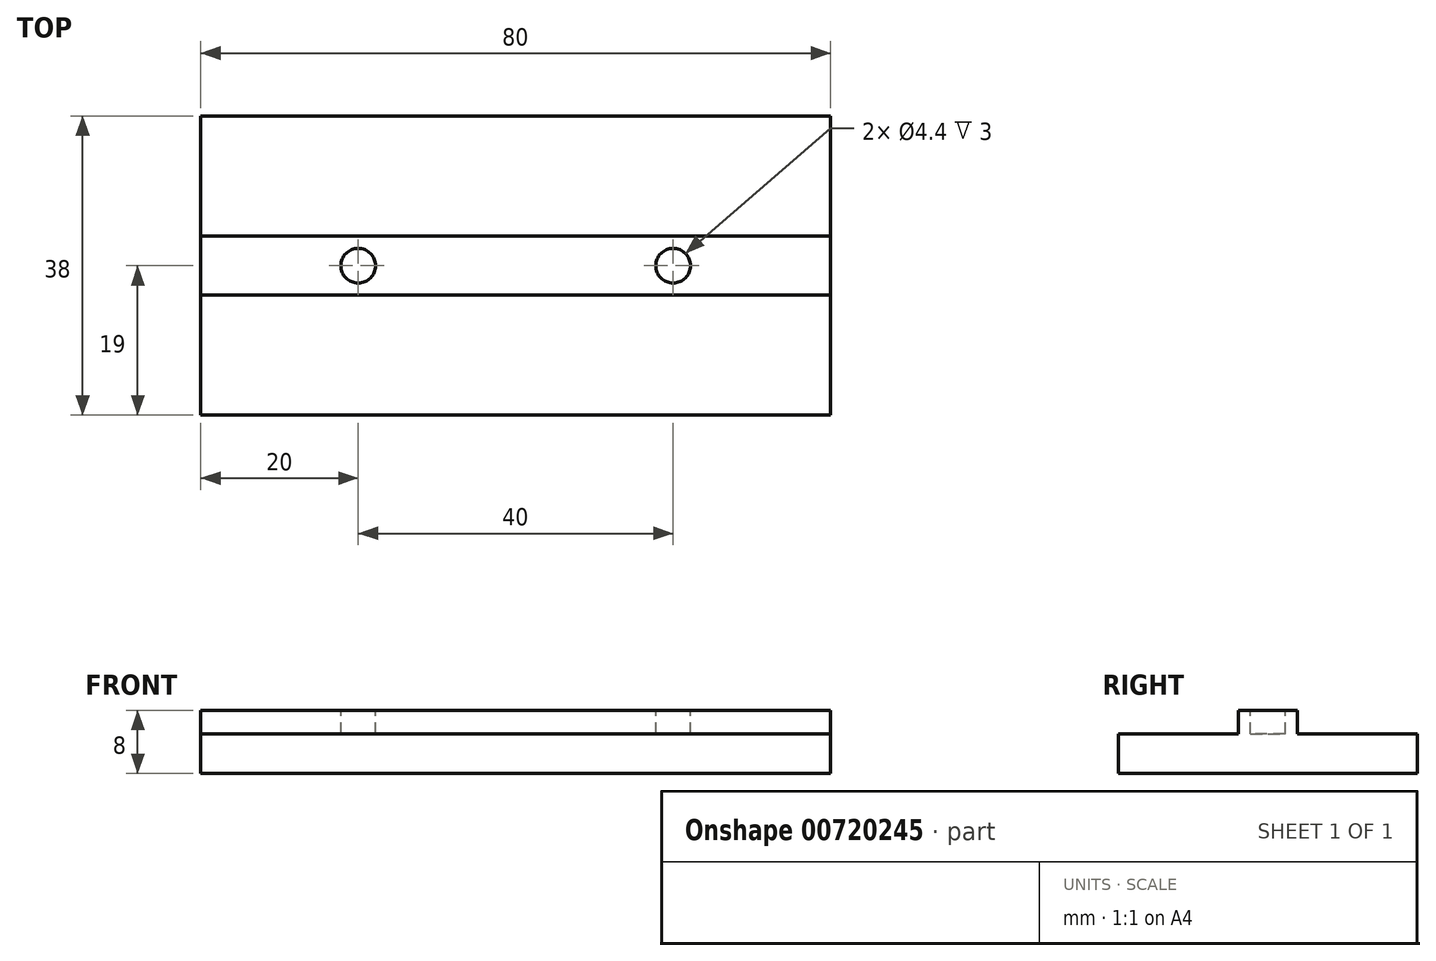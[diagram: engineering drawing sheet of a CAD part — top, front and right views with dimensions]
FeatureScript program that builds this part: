
annotation { "Feature Type Name" : "Feature", "Feature Type Description" : "" }
export const myFeature = defineFeature(function(context is Context, id is Id, definition is map)
    precondition{}
    {
        {
            var Q0;
            Q0=qCreatedBy(makeId("Top.planeOp"),FACE);
            var sketch = newSketch(context, id + "F0", { "sketchPlane" : qUnion([Q0])});
            skLineSegment(sketch, "E0.bottom", {"start": v(40, 19) * mm, "end": v(-40, 19) * mm});
            skLineSegment(sketch, "E0.top", {"start": v(40, -19) * mm, "end": v(-40, -19) * mm});
            skLineSegment(sketch, "E0.left", {"start": v(40, 19) * mm, "end": v(40, -19) * mm});
            skLineSegment(sketch, "E0.right", {"start": v(-40, 19) * mm, "end": v(-40, -19) * mm});
            skPoint(sketch, "E0.middle", {"position": v(0, 0) * mm});
            skLineSegment(sketch, "E1.bottom", {"start": v(40, 3.75) * mm, "end": v(-40, 3.75) * mm});
            skLineSegment(sketch, "E1.top", {"start": v(40, -3.75) * mm, "end": v(-40, -3.75) * mm});
            skLineSegment(sketch, "E1.left", {"start": v(40, 3.75) * mm, "end": v(40, -3.75) * mm});
            skLineSegment(sketch, "E1.right", {"start": v(-40, 3.75) * mm, "end": v(-40, -3.75) * mm});
            skSolve(sketch);
        }
        {
            var Q0;
            {var subQ0=sQuery(id+"F0.wireOp",EDGE,"E0.bottom");Q0=makeQuery(id+"F0.imprint","IMPRINT",FACE,{"disambiguationData":[TD([[makeQuery(id+"F0.imprint","IMPRINT",EDGE,{"derivedFrom":subQ0}),1.0]])]});}
            var Q1;
            {var subQ0=sQuery(id+"F0.wireOp",EDGE,"E0.top");Q1=makeQuery(id+"F0.imprint","IMPRINT",FACE,{"disambiguationData":[TD([[makeQuery(id+"F0.imprint","IMPRINT",EDGE,{"derivedFrom":subQ0}),-1.0]])]});}
            var Q2;
            Q2=makeQuery(id+"F0.imprint","IMPRINT",FACE,{"disambiguationData":[TD([[makeQuery(id+"F0.imprint","IMPRINT",EDGE,{"derivedFrom":sQuery(id+"F0.wireOp",EDGE,"E1.bottom")}),1.0]])]});
            extrude(context, id + "F1", {"entities" : qUnion([Q0, Q1, Q2]), "oppositeDirection" : true, "depth" : 5 * mm, "offsetDistance" : 25 * mm});
        }
        {
            var Q0;
            Q0=makeQuery(id+"F0.imprint","IMPRINT",FACE,{"disambiguationData":[TD([[makeQuery(id+"F0.imprint","IMPRINT",EDGE,{"derivedFrom":sQuery(id+"F0.wireOp",EDGE,"E1.bottom")}),1.0]])]});
            extrude(context, id + "F2", {"entities" : qUnion([Q0]), "operationType" : NewBodyOperationType.ADD, "depth" : 3 * mm, "offsetDistance" : 25 * mm});
        }
        {
            var Q0;
            {var subQ0=sQuery(id+"F0.wireOp",EDGE,"E0.top");Q0=makeQuery(id+"F0.imprint","IMPRINT",FACE,{"disambiguationData":[TD([[makeQuery(id+"F0.imprint","IMPRINT",EDGE,{"derivedFrom":subQ0}),-1.0]])]});}
            var sketch = newSketch(context, id + "F3", { "sketchPlane" : qUnion([Q0])});
            skPoint(sketch, "E2", {"position": v(-20, 0) * mm});
            skPoint(sketch, "E3", {"position": v(20, 0) * mm});
            skSolve(sketch);
        }
        {
            var Q0;
            Q0=sQuery(id+"F3.wireOp",VERTEX,"E2");
            var Q1;
            Q1=sQuery(id+"F3.wireOp",VERTEX,"E3");
            var Q2;
            Q2=makeQuery(id+"F1.opExtrude","SWEPT_BODY",BODY,{"disambiguationData":[OSD([sQuery(id+"F0.wireOp",EDGE,"E0.bottom"),sQuery(id+"F0.wireOp",EDGE,"E0.top"),sQuery(id+"F0.wireOp",EDGE,"E0.left"),sQuery(id+"F0.wireOp",EDGE,"E0.right"),sQuery(id+"F0.wireOp",EDGE,"E1.left"),sQuery(id+"F0.wireOp",EDGE,"E1.right")])]});
            hole(context, id + "F4", {"style" : HoleStyle.SIMPLE, "endStyle" : HoleEndStyle.THROUGH, "oppositeDirection" : true, "standardTappedOrClearance" : lookupTablePath({ "fit" : "Normal", "standard" : "ISO", "size" : "M4", "type" : "Clearance" }), "standardBlindInLast" : lookupTablePath({ "fit" : "Standard", "standard" : "ISO", "size" : "M4", "type" : "Clearance" }), "holeDiameter" : 4.4 * mm, "majorDiameter" : 5 * mm, "tappedDepth" : 12 * mm, "tapClearance" : 3, "locations" : qUnion([Q0, Q1]), "scope" : qUnion([Q2])});
        }
    });
